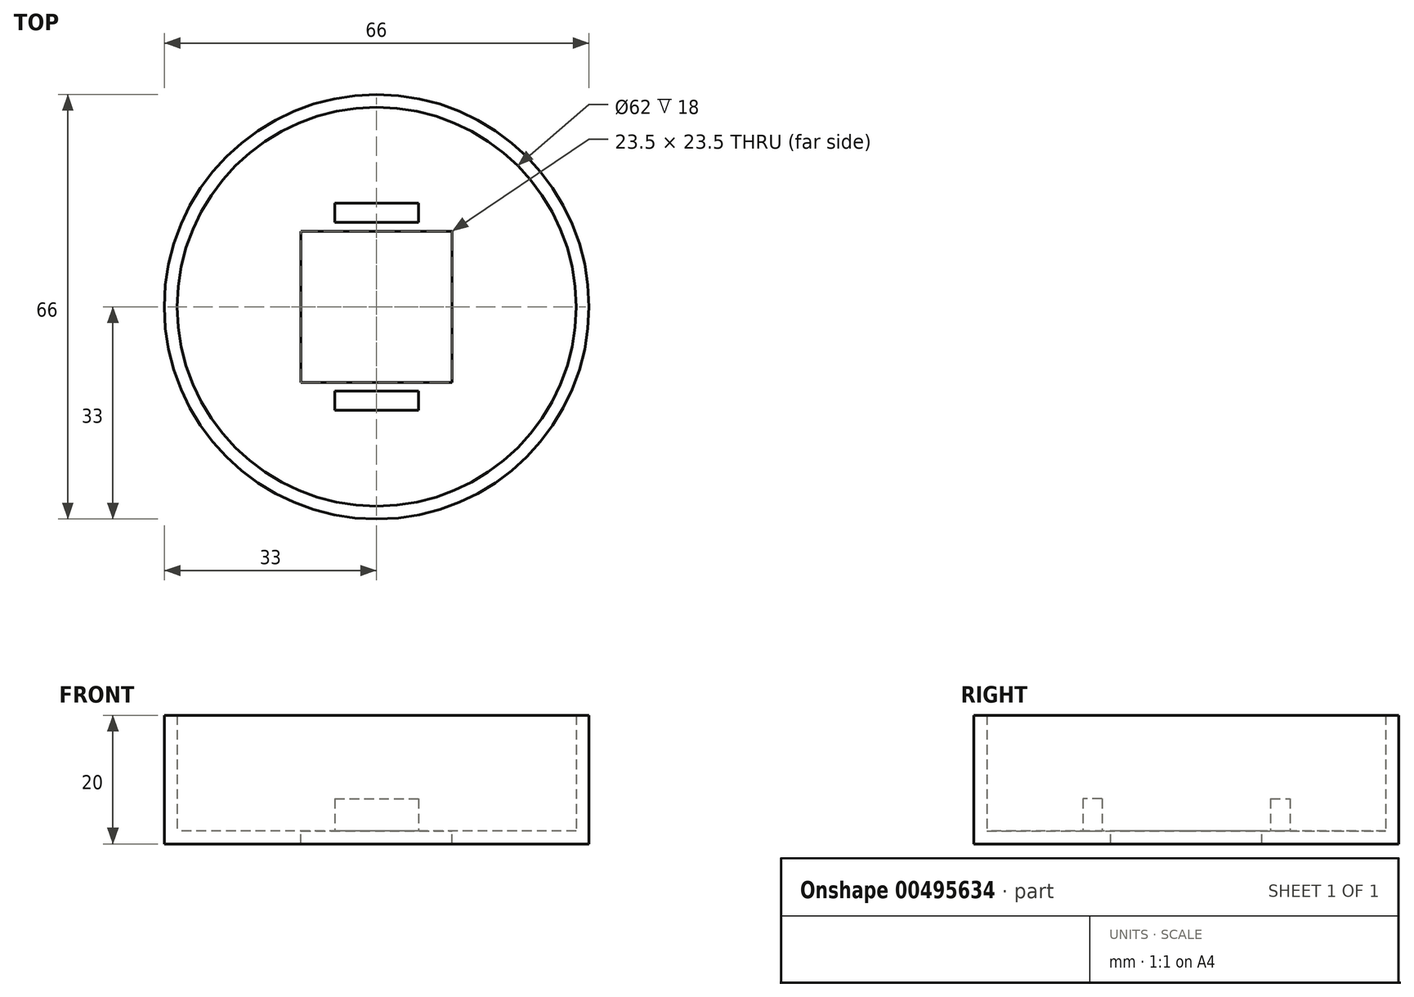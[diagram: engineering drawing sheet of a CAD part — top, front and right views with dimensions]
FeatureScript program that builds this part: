
annotation { "Feature Type Name" : "Feature", "Feature Type Description" : "" }
export const myFeature = defineFeature(function(context is Context, id is Id, definition is map)
    precondition{}
    {
        {
            var Q0;
            Q0=qCreatedBy(makeId("Top.planeOp"),FACE);
            var sketch = newSketch(context, id + "F0", { "sketchPlane" : qUnion([Q0])});
            skCircle(sketch, "E0", {"center": v(0, 0) * mm, "radius": 33 * mm});
            skSolve(sketch);
        }
        {
            var Q0;
            Q0=qSketchRegion(id+"F0",true);
            extrude(context, id + "F1", {"entities" : qUnion([Q0]), "depth" : 20 * mm});
        }
        {
            var Q0;
            Q0=makeQuery(id+"F1.opExtrude","CAP_FACE",FACE,{"disambiguationData":[OSD([sQuery(id+"F0.wireOp",EDGE,"E0")])],"isStart":false});
            shell(context, id + "F2", {"entities" : qUnion([Q0]), "thickness" : 2 * mm});
        }
        {
            var Q0;
            Q0=qSketchRegion(id+"F0",true);
            extrude(context, id + "F3", {"entities" : qUnion([Q0]), "operationType" : NewBodyOperationType.REMOVE, "endBound" : BoundingType.THROUGH_ALL, "oppositeDirection" : true, "depth" : 25 * mm});
        }
        {
            var Q0;
            Q0=makeQuery(id+"F0.imprint","IMPRINT",FACE,{"disambiguationData":[TD([[makeQuery(id+"F0.imprint","IMPRINT",EDGE,{"derivedFrom":sQuery(id+"F0.wireOp",EDGE,"E0")}),1.0]])]});
            var sketch = newSketch(context, id + "F4", { "sketchPlane" : qUnion([Q0])});
            skLineSegment(sketch, "E1.bottom", {"start": v(-11.75, 11.75) * mm, "end": v(11.75, 11.75) * mm});
            skLineSegment(sketch, "E1.top", {"start": v(-11.75, -11.75) * mm, "end": v(11.75, -11.75) * mm});
            skLineSegment(sketch, "E1.left", {"start": v(-11.75, 11.75) * mm, "end": v(-11.75, -11.75) * mm});
            skLineSegment(sketch, "E1.right", {"start": v(11.75, 11.75) * mm, "end": v(11.75, -11.75) * mm});
            skPoint(sketch, "E1.middle", {"position": v(0, 0) * mm});
            skSolve(sketch);
        }
        {
            var Q0;
            Q0=makeQuery(id+"F4.imprint","IMPRINT",FACE,{"disambiguationData":[TD([[makeQuery(id+"F4.imprint","IMPRINT",EDGE,{"derivedFrom":sQuery(id+"F4.wireOp",EDGE,"E1.bottom")}),-1.0]])]});
            extrude(context, id + "F5", {"entities" : qUnion([Q0]), "operationType" : NewBodyOperationType.REMOVE, "endBound" : BoundingType.SYMMETRIC, "oppositeDirection" : true, "depth" : 25 * mm});
        }
        {
            var Q0;
            Q0=qCreatedBy(makeId("Top.planeOp"),FACE);
            var sketch = newSketch(context, id + "F6", { "sketchPlane" : qUnion([Q0])});
            skLineSegment(sketch, "E2.bottom", {"start": v(-6.5, 13.1) * mm, "end": v(6.5, 13.1) * mm});
            skLineSegment(sketch, "E2.top", {"start": v(-6.5, 16.1) * mm, "end": v(6.5, 16.1) * mm});
            skLineSegment(sketch, "E2.left", {"start": v(-6.5, 13.1) * mm, "end": v(-6.5, 16.1) * mm});
            skLineSegment(sketch, "E2.right", {"start": v(6.5, 13.1) * mm, "end": v(6.5, 16.1) * mm});
            skPoint(sketch, "E2.middle", {"position": v(0, 14.6) * mm});
            skLineSegment(sketch, "E3.bottom", {"start": v(-6.5, -13.09) * mm, "end": v(6.5, -13.09) * mm});
            skLineSegment(sketch, "E3.top", {"start": v(-6.5, -16.09) * mm, "end": v(6.5, -16.09) * mm});
            skLineSegment(sketch, "E3.left", {"start": v(-6.5, -13.09) * mm, "end": v(-6.5, -16.09) * mm});
            skLineSegment(sketch, "E3.right", {"start": v(6.5, -13.09) * mm, "end": v(6.5, -16.09) * mm});
            skPoint(sketch, "E3.middle", {"position": v(0, -14.59) * mm});
            skSolve(sketch);
        }
        {
            var Q0;
            Q0=qSketchRegion(id+"F6",true);
            extrude(context, id + "F7", {"entities" : qUnion([Q0]), "operationType" : NewBodyOperationType.ADD, "depth" : 7 * mm});
        }
    });
